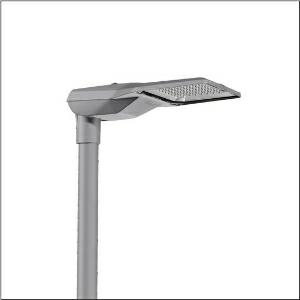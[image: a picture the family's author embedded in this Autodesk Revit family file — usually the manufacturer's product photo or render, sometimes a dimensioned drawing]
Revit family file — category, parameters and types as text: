
# Revit family: streetlight_sl_21_midi___st0_8a_5xe3c43s08lb_4b77
name_source: partatom
category: Lighting Fixtures
units: mm (PartAtom-declared; Revit-internal decimal feet)

## family parameters
Cut with Voids When Loaded = No
Host = Face
Light Source = No
Part Type = Normal
Room Calculation Point = No
Round Connector Dimension = Use Diameter
Shared = No

## types (1)
- --- (1 x LED, 14950 lm, 99.6 W, 4000K)
    Apparent Load = 100 VA
    CIE Flux Codes = 38 75 97 100 100
    Color Rendering = 70
    Color Temperature = 4000K
    Default Elevation = 1800 mm
    Description = Streetlight SL 21 midi, mast luminaire, primary light control with lens, of PMMA, primary optical cover: cover, of toughened safety glass, transparent, light distribution: ST0.8a, light emission: direct distribution, primary light characteristic: asymmetric, installation type: side-entry, post-top, LED, High Power LED, rated luminous flux: 14.950lm, luminous efficacy: 150lm/W, light colour: 740, colour temperature: 4000K, control gear: D4i, control: overheat protection, constant luminous flux control, time-dependent luminous flux control, flexible luminous flux parameterisation, pre-setting: logarithmic dimming characteristic, mains connection: 230..240V, AC, 50/60Hz, start of lifetime: 100W, end of service life: 102W, reduction: 46W, luminaire housing, of diecast aluminium, powder-coated, SITECO metallic grey (DB 702S), corrosivity category C5 high according to DIN EN ISO 12944, please order mast flange separately, inclination adjustable: 0°, 5°, 10°, 15°, sealing non-destructively replaceable, multi-level sealing system, length: 644mm, width: 335mm, height: 110mm, mast flange for spigot size: 42mm (side-entry): 5XC10008XM4, 60/48mm (side-entry/post-top): 5XC10108XM2, 76/60mm (side-entry/post-top): 5XC10108XM1, mounting height: 4..8m, Smart Interface above, protection rating (complete): IP66, insulation class (complete): insulation class II (safety insulation), certification: CE, ENEC, ENEC+, VDE, impact resistance: IK10, permissible operating ambient temperature for outdoor applications: -40..+50°C, standard-compliant lighting for roads and squares, packaging unit: 1 piece

Light Distribution: ST0.8a
    Height = 111 mm
    Lamp = 1 x LED
    Lamp Light Flux = 14950 lm
    Lamp Power = 99.6 W
    Lamp count = 1
    Length = 644 mm
    Luminous efficacy = 150 lm/W
    Manufacturer = Siteco
    ModVariant = No
    Model = 5XE3C43S08LB
    Number of Poles = 1
    OnlyDefault = Yes
    Power Factor = 1
    Product Name = Streetlight SL 21 midi | ST0.8a
    Product group = mast luminaire | pylon top
    ProductGroupID = 6100
    Protection Class = Protection class II
    Protection Degree = IP 66
    RLX_Detail_Level = 1
    RLX_Emergency_Light_Flux = 0 lm
    RLX_Emergency_Type = 0
    RLX_Emergency_Type_DB = No
    RlxData = <blob elided: 26837 chars, md5=8595602e>
    Socket = socket
    Standby Power = 0 W
    System Light Flux = 14950 lm
    System Power = 100 W
    Type Comments = factory setting: luminous flux: 100 % | dim-lin: 254 | 1020 mA
    Type Image = l_1004302.jpg
    URL = http://relux.com
    VarID = @adj_031045
    Voltage = 0 V
    Weight = 0.00 kg
    Width = 336 mm

## geometry (parser evidence)
native form markers: Blend x4, Sweep x11
no freeform markers — native parametric forms only
